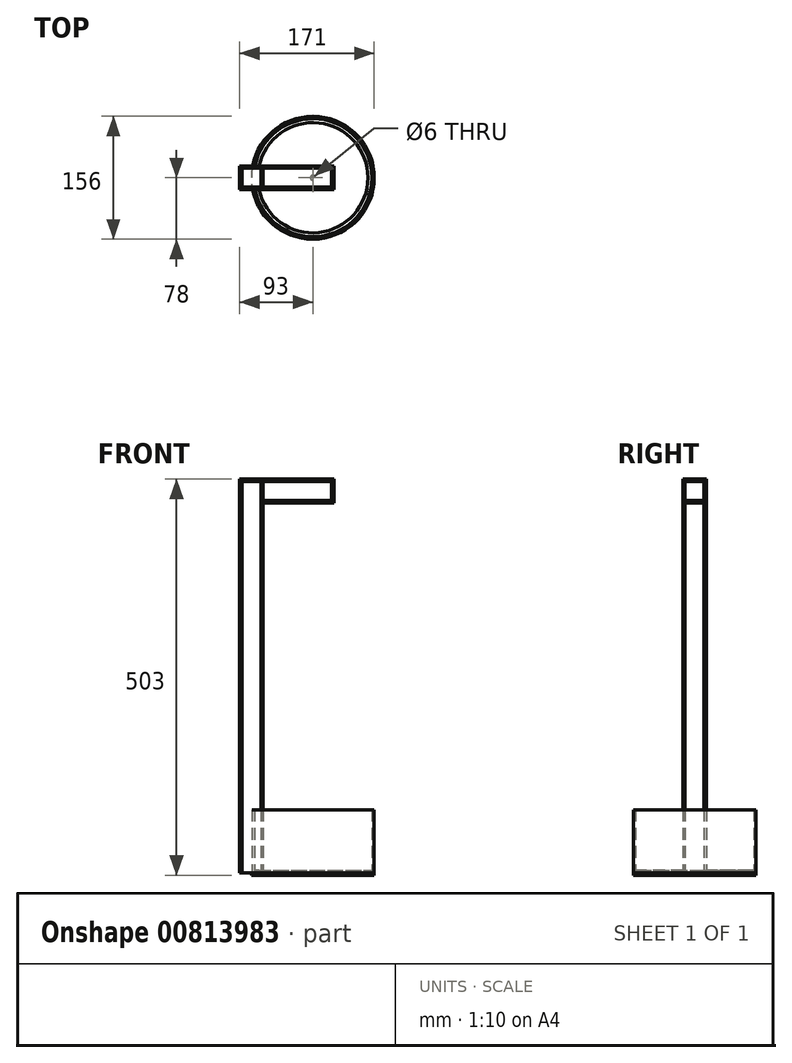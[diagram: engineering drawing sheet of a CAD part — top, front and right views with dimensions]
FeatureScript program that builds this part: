
annotation { "Feature Type Name" : "Feature", "Feature Type Description" : "" }
export const myFeature = defineFeature(function(context is Context, id is Id, definition is map)
    precondition{}
    {
        {
            assignVariable(context, id + "F0", {"variableType" : VariableType.LENGTH, "name" : "wt", "lengthValue" : 3 * mm});
        }
        {
            assignVariable(context, id + "F1", {"variableType" : VariableType.LENGTH, "name" : "armm", "lengthValue" : 30 * mm});
        }
        {
            assignVariable(context, id + "F2", {"variableType" : VariableType.LENGTH, "name" : "beamh", "lengthValue" : 500 * mm});
        }
        {
            assignVariable(context, id + "F3", {"variableType" : VariableType.LENGTH, "name" : "beaml", "lengthValue" : 90 * mm});
        }
        {
            var Q0;
            Q0=qCreatedBy(makeId("Top.planeOp"),FACE);
            var sketch = newSketch(context, id + "F4", { "sketchPlane" : qUnion([Q0])});
            skCircle(sketch, "E0", {"center": v(0, 0) * mm, "radius": 75 * mm});
            skCircle(sketch, "E1.0", {"center": v(0, 0) * mm, "radius": 78 * mm});
            skLineSegment(sketch, "E2", {"start": v(0, 0) * mm, "end": v(-78, 0) * mm, "construction": true});
            skLineSegment(sketch, "E3", {"start": v(0, -15) * mm, "end": v(-73.48, -15) * mm, "construction": true});
            skLineSegment(sketch, "E4.MirrorCS", {"start": v(0, 15) * mm, "end": v(-73.48, 15) * mm, "construction": true});
            skLineSegment(sketch, "E5.bottom", {"start": v(-63, -15) * mm, "end": v(-93, -15) * mm});
            skLineSegment(sketch, "E5.top", {"start": v(-63, 15) * mm, "end": v(-93, 15) * mm});
            skLineSegment(sketch, "E5.left", {"start": v(-63, -15) * mm, "end": v(-63, 15) * mm});
            skLineSegment(sketch, "E5.right", {"start": v(-93, -15) * mm, "end": v(-93, 15) * mm});
            skPoint(sketch, "E5.middle", {"position": v(-78, 0) * mm});
            skLineSegment(sketch, "E6.0", {"start": v(-90, -12) * mm, "end": v(-90, 12) * mm});
            skLineSegment(sketch, "E6.1", {"start": v(-66, -12) * mm, "end": v(-90, -12) * mm});
            skLineSegment(sketch, "E6.2", {"start": v(-66, -12) * mm, "end": v(-66, 12) * mm});
            skLineSegment(sketch, "E6.3", {"start": v(-66, 12) * mm, "end": v(-90, 12) * mm});
            skCircle(sketch, "E7", {"center": v(0, 0) * mm, "radius": 70 * mm});
            skLineSegment(sketch, "E8", {"start": v(-90, 12) * mm, "end": v(-90, 15) * mm});
            skLineSegment(sketch, "E9", {"start": v(-66, 12) * mm, "end": v(-66, 15) * mm});
            skLineSegment(sketch, "E10", {"start": v(-66, 12) * mm, "end": v(-63, 12) * mm});
            skLineSegment(sketch, "E11", {"start": v(-90, 12) * mm, "end": v(-93, 12) * mm});
            skLineSegment(sketch, "E12.MirrorCS", {"start": v(-66, -12) * mm, "end": v(-63, -12) * mm});
            skLineSegment(sketch, "E13.MirrorCS", {"start": v(-66, -12) * mm, "end": v(-66, -15) * mm});
            skLineSegment(sketch, "E14.MirrorCS", {"start": v(-90, -12) * mm, "end": v(-90, -15) * mm});
            skLineSegment(sketch, "E15.MirrorCS", {"start": v(-90, -12) * mm, "end": v(-93, -12) * mm});
            skSolve(sketch);
        }
        {
            var Q0;
            Q0=makeQuery(id+"F4.imprint","IMPRINT",FACE,{"disambiguationData":[TD([[makeQuery(id+"F4.imprint","IMPRINT",EDGE,{"derivedFrom":sQuery(id+"F4.wireOp",EDGE,"E0")}),1.0]])]});
            var Q1;
            Q1=makeQuery(id+"F4.imprint","IMPRINT",FACE,{"disambiguationData":[TD([[makeQuery(id+"F4.imprint","IMPRINT",EDGE,{"derivedFrom":sQuery(id+"F4.wireOp",EDGE,"E0")}),-1.0]])]});
            var Q2;
            {var subQ0=sQuery(id+"F4.wireOp",EDGE,"E6.2");Q2=makeQuery(id+"F4.imprint","IMPRINT",FACE,{"disambiguationData":[TD([[makeQuery(id+"F4.imprint","IMPRINT",EDGE,{"derivedFrom":subQ0}),1.0]])]});}
            var Q3;
            {var subQ4=sQuery(id+"F4.wireOp",EDGE,"E5.left");var subQ6=sQuery(id+"F4.wireOp",EDGE,"E5.bottom");var subQ9=makeQuery(id+"F4.imprint","INTERSECT",VERTEX,{"derivedFrom":[subQ6,subQ4]});Q3=makeQuery(id+"F4.imprint","IMPRINT",FACE,{"disambiguationData":[TD([[makeQuery(id+"F4.imprint","IMPRINT",EDGE,{"disambiguationData":[TD([[subQ9,-1.0]])],"derivedFrom":subQ6}),1.0]])]});}
            var Q4;
            {var subQ0=sQuery(id+"F4.wireOp",EDGE,"E9");Q4=makeQuery(id+"F4.imprint","IMPRINT",FACE,{"disambiguationData":[TD([[makeQuery(id+"F4.imprint","IMPRINT",EDGE,{"derivedFrom":subQ0}),1.0]])]});}
            var Q5;
            Q5=makeQuery(id+"F4.imprint","IMPRINT",FACE,{"disambiguationData":[TD([[makeQuery(id+"F4.imprint","IMPRINT",EDGE,{"derivedFrom":sQuery(id+"F4.wireOp",EDGE,"E6.2")}),-1.0]])]});
            var Q6;
            {var subQ3=sQuery(id+"F4.wireOp",EDGE,"E9");Q6=makeQuery(id+"F4.imprint","IMPRINT",FACE,{"disambiguationData":[TD([[makeQuery(id+"F4.imprint","IMPRINT",EDGE,{"derivedFrom":subQ3}),-1.0]])]});}
            var Q7;
            {var subQ0=sQuery(id+"F4.wireOp",EDGE,"E13.MirrorCS");Q7=makeQuery(id+"F4.imprint","IMPRINT",FACE,{"disambiguationData":[TD([[makeQuery(id+"F4.imprint","IMPRINT",EDGE,{"derivedFrom":subQ0}),-1.0]])]});}
            var Q8;
            {var subQ4=sQuery(id+"F4.wireOp",EDGE,"E12.MirrorCS");Q8=makeQuery(id+"F4.imprint","IMPRINT",FACE,{"disambiguationData":[TD([[makeQuery(id+"F4.imprint","IMPRINT",EDGE,{"derivedFrom":subQ4}),-1.0]])]});}
            extrude(context, id + "F5", {"entities" : qUnion([Q0, Q1, Q2, Q3, Q4, Q5, Q6, Q7, Q8]), "oppositeDirection" : true, "depth" : getVariable(context, 'wt'), "offsetDistance" : 25 * mm});
        }
        {
            var Q0;
            {var subQ0=sQuery(id+"F4.wireOp",EDGE,"E5.top");var subQ1=sQuery(id+"F4.wireOp",EDGE,"E0");var subQ2=makeQuery(id+"F4.imprint","INTERSECT",VERTEX,{"derivedFrom":[subQ1,subQ0]});Q0=makeQuery(id+"F4.imprint","IMPRINT",FACE,{"disambiguationData":[TD([[makeQuery(id+"F4.imprint","IMPRINT",EDGE,{"disambiguationData":[TD([[subQ2,1.0]])],"derivedFrom":subQ1}),1.0]])]});}
            extrude(context, id + "F6", {"entities" : qUnion([Q0]), "depth" : getVariable(context, 'wt'), "offsetDistance" : 25 * mm});
        }
        {
            var Q0;
            {var subQ0=sQuery(id+"F4.wireOp",EDGE,"E5.top");var subQ1=sQuery(id+"F4.wireOp",EDGE,"E0");var subQ2=makeQuery(id+"F4.imprint","INTERSECT",VERTEX,{"derivedFrom":[subQ1,subQ0]});Q0=makeQuery(id+"F4.imprint","IMPRINT",FACE,{"disambiguationData":[TD([[makeQuery(id+"F4.imprint","IMPRINT",EDGE,{"disambiguationData":[TD([[subQ2,1.0]])],"derivedFrom":subQ1}),-1.0]])]});}
            var Q1;
            {var subQ0=sQuery(id+"F4.wireOp",EDGE,"E6.3");var subQ1=sQuery(id+"F4.wireOp",EDGE,"E0");var subQ2=makeQuery(id+"F4.imprint","INTERSECT",VERTEX,{"derivedFrom":[subQ1,subQ0]});Q1=makeQuery(id+"F4.imprint","IMPRINT",FACE,{"disambiguationData":[TD([[makeQuery(id+"F4.imprint","IMPRINT",EDGE,{"disambiguationData":[TD([[subQ2,1.0]])],"derivedFrom":subQ1}),-1.0]])]});}
            var Q2;
            {var subQ0=sQuery(id+"F4.wireOp",EDGE,"E6.1");var subQ1=sQuery(id+"F4.wireOp",EDGE,"E0");var subQ2=makeQuery(id+"F4.imprint","INTERSECT",VERTEX,{"derivedFrom":[subQ1,subQ0]});Q2=makeQuery(id+"F4.imprint","IMPRINT",FACE,{"disambiguationData":[TD([[makeQuery(id+"F4.imprint","IMPRINT",EDGE,{"disambiguationData":[TD([[subQ2,-1.0]])],"derivedFrom":subQ1}),-1.0]])]});}
            extrude(context, id + "F7", {"entities" : qUnion([Q0, Q1, Q2]), "depth" : 80 * mm, "offsetDistance" : 25 * mm});
        }
        {
            var Q0;
            {var subQ5=sQuery(id+"F4.wireOp",EDGE,"E8");Q0=makeQuery(id+"F4.imprint","IMPRINT",FACE,{"disambiguationData":[TD([[makeQuery(id+"F4.imprint","IMPRINT",EDGE,{"derivedFrom":subQ5}),-1.0]])]});}
            var Q1;
            {var subQ0=sQuery(id+"F4.wireOp",EDGE,"E6.3");var subQ1=sQuery(id+"F4.wireOp",EDGE,"E0");var subQ2=makeQuery(id+"F4.imprint","INTERSECT",VERTEX,{"derivedFrom":[subQ1,subQ0]});Q1=makeQuery(id+"F4.imprint","IMPRINT",FACE,{"disambiguationData":[TD([[makeQuery(id+"F4.imprint","IMPRINT",EDGE,{"disambiguationData":[TD([[subQ2,1.0]])],"derivedFrom":subQ1}),-1.0]])]});}
            var Q2;
            {var subQ0=sQuery(id+"F4.wireOp",EDGE,"E6.3");var subQ1=sQuery(id+"F4.wireOp",EDGE,"E0");var subQ2=makeQuery(id+"F4.imprint","INTERSECT",VERTEX,{"derivedFrom":[subQ1,subQ0]});Q2=makeQuery(id+"F4.imprint","IMPRINT",FACE,{"disambiguationData":[TD([[makeQuery(id+"F4.imprint","IMPRINT",EDGE,{"disambiguationData":[TD([[subQ2,1.0]])],"derivedFrom":subQ1}),1.0]])]});}
            var Q3;
            {var subQ0=sQuery(id+"F4.wireOp",EDGE,"E9");Q3=makeQuery(id+"F4.imprint","IMPRINT",FACE,{"disambiguationData":[TD([[makeQuery(id+"F4.imprint","IMPRINT",EDGE,{"derivedFrom":subQ0}),1.0]])]});}
            var Q4;
            {var subQ3=sQuery(id+"F4.wireOp",EDGE,"E9");Q4=makeQuery(id+"F4.imprint","IMPRINT",FACE,{"disambiguationData":[TD([[makeQuery(id+"F4.imprint","IMPRINT",EDGE,{"derivedFrom":subQ3}),-1.0]])]});}
            var Q5;
            {var subQ4=sQuery(id+"F4.wireOp",EDGE,"E12.MirrorCS");Q5=makeQuery(id+"F4.imprint","IMPRINT",FACE,{"disambiguationData":[TD([[makeQuery(id+"F4.imprint","IMPRINT",EDGE,{"derivedFrom":subQ4}),-1.0]])]});}
            var Q6;
            {var subQ0=sQuery(id+"F4.wireOp",EDGE,"E13.MirrorCS");Q6=makeQuery(id+"F4.imprint","IMPRINT",FACE,{"disambiguationData":[TD([[makeQuery(id+"F4.imprint","IMPRINT",EDGE,{"derivedFrom":subQ0}),-1.0]])]});}
            var Q7;
            {var subQ0=sQuery(id+"F4.wireOp",EDGE,"E6.1");var subQ1=sQuery(id+"F4.wireOp",EDGE,"E0");var subQ2=makeQuery(id+"F4.imprint","INTERSECT",VERTEX,{"derivedFrom":[subQ1,subQ0]});Q7=makeQuery(id+"F4.imprint","IMPRINT",FACE,{"disambiguationData":[TD([[makeQuery(id+"F4.imprint","IMPRINT",EDGE,{"disambiguationData":[TD([[subQ2,-1.0]])],"derivedFrom":subQ1}),1.0]])]});}
            var Q8;
            {var subQ0=sQuery(id+"F4.wireOp",EDGE,"E6.1");var subQ1=sQuery(id+"F4.wireOp",EDGE,"E0");var subQ2=makeQuery(id+"F4.imprint","INTERSECT",VERTEX,{"derivedFrom":[subQ1,subQ0]});Q8=makeQuery(id+"F4.imprint","IMPRINT",FACE,{"disambiguationData":[TD([[makeQuery(id+"F4.imprint","IMPRINT",EDGE,{"disambiguationData":[TD([[subQ2,-1.0]])],"derivedFrom":subQ1}),-1.0]])]});}
            var Q9;
            {var subQ5=sQuery(id+"F4.wireOp",EDGE,"E14.MirrorCS");Q9=makeQuery(id+"F4.imprint","IMPRINT",FACE,{"disambiguationData":[TD([[makeQuery(id+"F4.imprint","IMPRINT",EDGE,{"derivedFrom":subQ5}),1.0]])]});}
            var Q10;
            {var subQ3=sQuery(id+"F4.wireOp",EDGE,"E14.MirrorCS");Q10=makeQuery(id+"F4.imprint","IMPRINT",FACE,{"disambiguationData":[TD([[makeQuery(id+"F4.imprint","IMPRINT",EDGE,{"derivedFrom":subQ3}),-1.0]])]});}
            var Q11;
            {var subQ3=sQuery(id+"F4.wireOp",EDGE,"E8");Q11=makeQuery(id+"F4.imprint","IMPRINT",FACE,{"disambiguationData":[TD([[makeQuery(id+"F4.imprint","IMPRINT",EDGE,{"derivedFrom":subQ3}),1.0]])]});}
            extrude(context, id + "F8", {"entities" : qUnion([Q0, Q1, Q2, Q3, Q4, Q5, Q6, Q7, Q8, Q9, Q10, Q11]), "depth" : getVariable(context, 'beamh'), "offsetDistance" : 25 * mm});
        }
        {
            var Q0;
            Q0=makeQuery(id+"F4.imprint","IMPRINT",FACE,{"disambiguationData":[TD([[makeQuery(id+"F4.imprint","IMPRINT",EDGE,{"derivedFrom":sQuery(id+"F4.wireOp",EDGE,"E6.0")}),1.0]])]});
            var Q1;
            {var subQ3=sQuery(id+"F4.wireOp",EDGE,"E14.MirrorCS");Q1=makeQuery(id+"F4.imprint","IMPRINT",FACE,{"disambiguationData":[TD([[makeQuery(id+"F4.imprint","IMPRINT",EDGE,{"derivedFrom":subQ3}),-1.0]])]});}
            var Q2;
            {var subQ3=sQuery(id+"F4.wireOp",EDGE,"E8");Q2=makeQuery(id+"F4.imprint","IMPRINT",FACE,{"disambiguationData":[TD([[makeQuery(id+"F4.imprint","IMPRINT",EDGE,{"derivedFrom":subQ3}),1.0]])]});}
            extrude(context, id + "F9", {"entities" : qUnion([Q0, Q1, Q2]), "depth" : 500 * mm, "offsetDistance" : 25 * mm});
        }
        {
            var Q0;
            Q0=makeQuery(id+"F4.imprint","IMPRINT",FACE,{"disambiguationData":[TD([[makeQuery(id+"F4.imprint","IMPRINT",EDGE,{"derivedFrom":sQuery(id+"F4.wireOp",EDGE,"E6.2")}),-1.0]])]});
            var Q1;
            {var subQ4=sQuery(id+"F4.wireOp",EDGE,"E12.MirrorCS");Q1=makeQuery(id+"F4.imprint","IMPRINT",FACE,{"disambiguationData":[TD([[makeQuery(id+"F4.imprint","IMPRINT",EDGE,{"derivedFrom":subQ4}),-1.0]])]});}
            var Q2;
            {var subQ3=sQuery(id+"F4.wireOp",EDGE,"E9");Q2=makeQuery(id+"F4.imprint","IMPRINT",FACE,{"disambiguationData":[TD([[makeQuery(id+"F4.imprint","IMPRINT",EDGE,{"derivedFrom":subQ3}),-1.0]])]});}
            extrude(context, id + "F10", {"entities" : qUnion([Q0, Q1, Q2]), "depth" : getVariable(context, 'beamh') - getVariable(context, 'armm') + getVariable(context, 'wt'), "offsetDistance" : 25 * mm});
        }
        {
            var Q0;
            {var subQ0=sQuery(id+"F4.wireOp",EDGE,"E5.left");Q0=makeQuery(id+"F8.opExtrude","SWEPT_FACE",FACE,{"disambiguationData":[OSD([subQ0]),TDD([makeQuery(id+"F4.imprint","IMPRINT",EDGE,{"disambiguationData":[TD([[makeQuery(id+"F4.imprint","INTERSECT",VERTEX,{"derivedFrom":[sQuery(id+"F4.wireOp",EDGE,"E5.bottom"),subQ0]}),-1.0]])],"derivedFrom":subQ0})])]});}
            var sketch = newSketch(context, id + "F11", { "sketchPlane" : qUnion([Q0])});
            skLineSegment(sketch, "E16.0", {"start": v(15, 500) * mm, "end": v(15, 0) * mm});
            skLineSegment(sketch, "E16.1", {"start": v(-15, 500) * mm, "end": v(15, 500) * mm});
            skLineSegment(sketch, "E17.0", {"start": v(-15, 473) * mm, "end": v(15, 473) * mm});
            skLineSegment(sketch, "E18", {"start": v(-15, 470) * mm, "end": v(15, 470) * mm});
            skLineSegment(sketch, "E19.0", {"start": v(-12, 500) * mm, "end": v(-12, 0) * mm});
            skLineSegment(sketch, "E20.0", {"start": v(12, 500) * mm, "end": v(12, 0) * mm});
            skLineSegment(sketch, "E21.0", {"start": v(-15, 500) * mm, "end": v(-15, 0) * mm});
            skLineSegment(sketch, "E22", {"start": v(-15, 497) * mm, "end": v(15, 497) * mm});
            skSolve(sketch);
        }
        {
            var Q0;
            {var subQ0=sQuery(id+"F11.wireOp",EDGE,"E21.0");var subQ1=sQuery(id+"F11.wireOp",EDGE,"E17.0");var subQ2=makeQuery(id+"F11.imprint","INTERSECT",VERTEX,{"derivedFrom":[subQ1,subQ0]});Q0=makeQuery(id+"F11.imprint","IMPRINT",FACE,{"disambiguationData":[TD([[makeQuery(id+"F11.imprint","IMPRINT",EDGE,{"disambiguationData":[TD([[subQ2,-1.0]])],"derivedFrom":subQ1}),1.0]])]});}
            var Q1;
            {var subQ0=sQuery(id+"F11.wireOp",EDGE,"E21.0");var subQ1=sQuery(id+"F11.wireOp",EDGE,"E16.1");var subQ2=makeQuery(id+"F11.imprint","INTERSECT",VERTEX,{"derivedFrom":[subQ1,subQ0]});Q1=makeQuery(id+"F11.imprint","IMPRINT",FACE,{"disambiguationData":[TD([[makeQuery(id+"F11.imprint","IMPRINT",EDGE,{"disambiguationData":[TD([[subQ2,-1.0]])],"derivedFrom":subQ1}),-1.0]])]});}
            var Q2;
            {var subQ0=sQuery(id+"F11.wireOp",EDGE,"E21.0");var subQ1=sQuery(id+"F11.wireOp",EDGE,"E17.0");var subQ2=makeQuery(id+"F11.imprint","INTERSECT",VERTEX,{"derivedFrom":[subQ1,subQ0]});Q2=makeQuery(id+"F11.imprint","IMPRINT",FACE,{"disambiguationData":[TD([[makeQuery(id+"F11.imprint","IMPRINT",EDGE,{"disambiguationData":[TD([[subQ2,-1.0]])],"derivedFrom":subQ1}),-1.0]])]});}
            var Q3;
            {var subQ0=sQuery(id+"F11.wireOp",EDGE,"E16.1");var subQ1=sQuery(id+"F11.wireOp",EDGE,"E16.0");var subQ2=makeQuery(id+"F11.imprint","INTERSECT",VERTEX,{"derivedFrom":[subQ1,subQ0]});Q3=makeQuery(id+"F11.imprint","IMPRINT",FACE,{"disambiguationData":[TD([[makeQuery(id+"F11.imprint","IMPRINT",EDGE,{"disambiguationData":[TD([[subQ2,-1.0]])],"derivedFrom":subQ1}),-1.0]])]});}
            var Q4;
            {var subQ0=sQuery(id+"F11.wireOp",EDGE,"E17.0");var subQ1=sQuery(id+"F11.wireOp",EDGE,"E16.0");var subQ2=makeQuery(id+"F11.imprint","INTERSECT",VERTEX,{"derivedFrom":[subQ1,subQ0]});Q4=makeQuery(id+"F11.imprint","IMPRINT",FACE,{"disambiguationData":[TD([[makeQuery(id+"F11.imprint","IMPRINT",EDGE,{"disambiguationData":[TD([[subQ2,1.0]])],"derivedFrom":subQ1}),-1.0]])]});}
            var Q5;
            {var subQ0=sQuery(id+"F11.wireOp",EDGE,"E17.0");var subQ1=sQuery(id+"F11.wireOp",EDGE,"E16.0");var subQ2=makeQuery(id+"F11.imprint","INTERSECT",VERTEX,{"derivedFrom":[subQ1,subQ0]});Q5=makeQuery(id+"F11.imprint","IMPRINT",FACE,{"disambiguationData":[TD([[makeQuery(id+"F11.imprint","IMPRINT",EDGE,{"disambiguationData":[TD([[subQ2,-1.0]])],"derivedFrom":subQ1}),-1.0]])]});}
            extrude(context, id + "F12", {"entities" : qUnion([Q0, Q1, Q2, Q3, Q4, Q5]), "depth" : getVariable(context, 'beaml'), "offsetDistance" : 25 * mm, "hasSecondDirection" : true, "secondDirectionOppositeDirection" : true, "secondDirectionDepth" : getVariable(context, 'wt')});
        }
        {
            var Q0;
            {var subQ0=sQuery(id+"F11.wireOp",EDGE,"E19.0");var subQ1=sQuery(id+"F11.wireOp",EDGE,"E16.1");var subQ2=makeQuery(id+"F11.imprint","INTERSECT",VERTEX,{"derivedFrom":[subQ1,subQ0]});Q0=makeQuery(id+"F11.imprint","IMPRINT",FACE,{"disambiguationData":[TD([[makeQuery(id+"F11.imprint","IMPRINT",EDGE,{"disambiguationData":[TD([[subQ2,-1.0]])],"derivedFrom":subQ1}),-1.0]])]});}
            var Q1;
            {var subQ0=sQuery(id+"F11.wireOp",EDGE,"E21.0");var subQ1=sQuery(id+"F11.wireOp",EDGE,"E16.1");var subQ2=makeQuery(id+"F11.imprint","INTERSECT",VERTEX,{"derivedFrom":[subQ1,subQ0]});Q1=makeQuery(id+"F11.imprint","IMPRINT",FACE,{"disambiguationData":[TD([[makeQuery(id+"F11.imprint","IMPRINT",EDGE,{"disambiguationData":[TD([[subQ2,-1.0]])],"derivedFrom":subQ1}),-1.0]])]});}
            var Q2;
            {var subQ0=sQuery(id+"F11.wireOp",EDGE,"E16.1");var subQ1=sQuery(id+"F11.wireOp",EDGE,"E16.0");var subQ2=makeQuery(id+"F11.imprint","INTERSECT",VERTEX,{"derivedFrom":[subQ1,subQ0]});Q2=makeQuery(id+"F11.imprint","IMPRINT",FACE,{"disambiguationData":[TD([[makeQuery(id+"F11.imprint","IMPRINT",EDGE,{"disambiguationData":[TD([[subQ2,-1.0]])],"derivedFrom":subQ1}),-1.0]])]});}
            var Q3;
            {var subQ0=sQuery(id+"F11.wireOp",EDGE,"E17.0");var subQ1=sQuery(id+"F11.wireOp",EDGE,"E16.0");var subQ2=makeQuery(id+"F11.imprint","INTERSECT",VERTEX,{"derivedFrom":[subQ1,subQ0]});Q3=makeQuery(id+"F11.imprint","IMPRINT",FACE,{"disambiguationData":[TD([[makeQuery(id+"F11.imprint","IMPRINT",EDGE,{"disambiguationData":[TD([[subQ2,-1.0]])],"derivedFrom":subQ1}),-1.0]])]});}
            var Q4;
            {var subQ0=sQuery(id+"F11.wireOp",EDGE,"E19.0");var subQ1=sQuery(id+"F11.wireOp",EDGE,"E17.0");var subQ2=makeQuery(id+"F11.imprint","INTERSECT",VERTEX,{"derivedFrom":[subQ1,subQ0]});Q4=makeQuery(id+"F11.imprint","IMPRINT",FACE,{"disambiguationData":[TD([[makeQuery(id+"F11.imprint","IMPRINT",EDGE,{"disambiguationData":[TD([[subQ2,-1.0]])],"derivedFrom":subQ1}),-1.0]])]});}
            var Q5;
            {var subQ0=sQuery(id+"F11.wireOp",EDGE,"E21.0");var subQ1=sQuery(id+"F11.wireOp",EDGE,"E17.0");var subQ2=makeQuery(id+"F11.imprint","INTERSECT",VERTEX,{"derivedFrom":[subQ1,subQ0]});Q5=makeQuery(id+"F11.imprint","IMPRINT",FACE,{"disambiguationData":[TD([[makeQuery(id+"F11.imprint","IMPRINT",EDGE,{"disambiguationData":[TD([[subQ2,-1.0]])],"derivedFrom":subQ1}),-1.0]])]});}
            extrude(context, id + "F13", {"entities" : qUnion([Q0, Q1, Q2, Q3, Q4, Q5]), "depth" : getVariable(context, 'beaml'), "offsetDistance" : 25 * mm, "hasSecondDirection" : true, "secondDirectionOppositeDirection" : true, "secondDirectionDepth" : getVariable(context, 'wt')});
        }
        {
            var Q0;
            Q0=makeQuery(id+"F13.opExtrude","CAP_FACE",FACE,{"disambiguationData":[OSD([sQuery(id+"F11.wireOp",EDGE,"E16.0"),sQuery(id+"F11.wireOp",EDGE,"E16.1"),sQuery(id+"F11.wireOp",EDGE,"E21.0"),sQuery(id+"F11.wireOp",EDGE,"E22")])],"isStart":false});
            var sketch = newSketch(context, id + "F14", { "sketchPlane" : qUnion([Q0])});
            skLineSegment(sketch, "E23.0", {"start": v(-15, 500) * mm, "end": v(-15, 470) * mm});
            skLineSegment(sketch, "E23.1", {"start": v(-15, 500) * mm, "end": v(15, 500) * mm});
            skLineSegment(sketch, "E23.2", {"start": v(15, 500) * mm, "end": v(15, 470) * mm});
            skLineSegment(sketch, "E23.3", {"start": v(-15, 470) * mm, "end": v(15, 470) * mm});
            skSolve(sketch);
        }
        {
            var Q0;
            {var subQ2=sQuery(id+"F14.wireOp",EDGE,"E23.3");Q0=makeQuery(id+"F14.imprint","IMPRINT",FACE,{"disambiguationData":[TD([[makeQuery(id+"F14.imprint","IMPRINT",EDGE,{"derivedFrom":subQ2}),1.0]])]});}
            var Q1;
            {var subQ0=sQuery(id+"F14.wireOp",EDGE,"E23.1");Q1=makeQuery(id+"F14.imprint","IMPRINT",FACE,{"disambiguationData":[TD([[makeQuery(id+"F14.imprint","IMPRINT",EDGE,{"derivedFrom":subQ0}),-1.0]])]});}
            extrude(context, id + "F15", {"entities" : qUnion([Q0, Q1]), "oppositeDirection" : true, "depth" : getVariable(context, 'wt'), "offsetDistance" : 25 * mm});
        }
        {
            var Q0;
            Q0=makeQuery(id+"F9.opExtrude","CAP_FACE",FACE,{"disambiguationData":[OSD([sQuery(id+"F4.wireOp",EDGE,"E5.bottom"),sQuery(id+"F4.wireOp",EDGE,"E5.top"),sQuery(id+"F4.wireOp",EDGE,"E5.right"),sQuery(id+"F4.wireOp",EDGE,"E6.0"),sQuery(id+"F4.wireOp",EDGE,"E8"),sQuery(id+"F4.wireOp",EDGE,"E14.MirrorCS")])],"isStart":false});
            var sketch = newSketch(context, id + "F16", { "sketchPlane" : qUnion([Q0])});
            skLineSegment(sketch, "E24.0", {"start": v(-93, -15) * mm, "end": v(-93, 15) * mm});
            skLineSegment(sketch, "E24.1", {"start": v(-63, -15) * mm, "end": v(-93, -15) * mm});
            skLineSegment(sketch, "E24.2", {"start": v(-63, 15) * mm, "end": v(-93, 15) * mm});
            skLineSegment(sketch, "E25", {"start": v(-63, -15) * mm, "end": v(-63, 15) * mm});
            skSolve(sketch);
        }
        {
            var Q0;
            {var subQ2=sQuery(id+"F16.wireOp",EDGE,"E25");Q0=makeQuery(id+"F16.imprint","IMPRINT",FACE,{"disambiguationData":[TD([[makeQuery(id+"F16.imprint","IMPRINT",EDGE,{"derivedFrom":subQ2}),1.0]])]});}
            var Q1;
            {var subQ0=sQuery(id+"F16.wireOp",EDGE,"E24.0");Q1=makeQuery(id+"F16.imprint","IMPRINT",FACE,{"disambiguationData":[TD([[makeQuery(id+"F16.imprint","IMPRINT",EDGE,{"derivedFrom":subQ0}),-1.0]])]});}
            extrude(context, id + "F17", {"entities" : qUnion([Q0, Q1]), "oppositeDirection" : true, "depth" : getVariable(context, 'wt'), "offsetDistance" : 25 * mm});
        }
        {
            var Q0;
            Q0=makeQuery(id+"F5.opExtrude","CAP_FACE",FACE,{"disambiguationData":[OSD([sQuery(id+"F4.wireOp",EDGE,"E1.0")])],"isStart":false});
            var sketch = newSketch(context, id + "F18", { "sketchPlane" : qUnion([Q0])});
            skCircle(sketch, "E26", {"center": v(0, 0) * mm, "radius": 3 * mm});
            skSolve(sketch);
        }
        {
            var Q0;
            Q0=makeQuery(id+"F18.imprint","IMPRINT",FACE,{"disambiguationData":[TD([[makeQuery(id+"F18.imprint","IMPRINT",EDGE,{"derivedFrom":sQuery(id+"F18.wireOp",EDGE,"E26")}),1.0]])]});
            extrude(context, id + "F19", {"entities" : qUnion([Q0]), "oppositeDirection" : true, "depth" : 488 * mm, "offsetDistance" : 25 * mm});
        }
        {
            var Q0;
            Q0=makeQuery(id+"F19.opExtrude","SWEPT_BODY",BODY,{"disambiguationData":[OSD([sQuery(id+"F18.wireOp",EDGE,"E26")])]});
            var Q1;
            Q1=makeQuery(id+"F13.opExtrude","SWEPT_BODY",BODY,{"disambiguationData":[OSD([sQuery(id+"F11.wireOp",EDGE,"E16.0"),sQuery(id+"F11.wireOp",EDGE,"E17.0"),sQuery(id+"F11.wireOp",EDGE,"E18"),sQuery(id+"F11.wireOp",EDGE,"E21.0")])]});
            booleanBodies(context, id + "F20", {"operationType" : BooleanOperationType.SUBTRACTION, "tools" : qUnion([Q0]), "targets" : qUnion([Q1])});
        }
        {
            var Q0;
            Q0=makeQuery(id+"F13.opExtrude","SWEPT_FACE",FACE,{"disambiguationData":[OSD([sQuery(id+"F11.wireOp",EDGE,"E18")])]});
            cPlane(context, id + "F21", {"entities" : qUnion([Q0]), "cplaneType" : CPlaneType.OFFSET, "offset" : 25 * mm, "width" : 150 * mm, "height" : 150 * mm});
        }
    });
